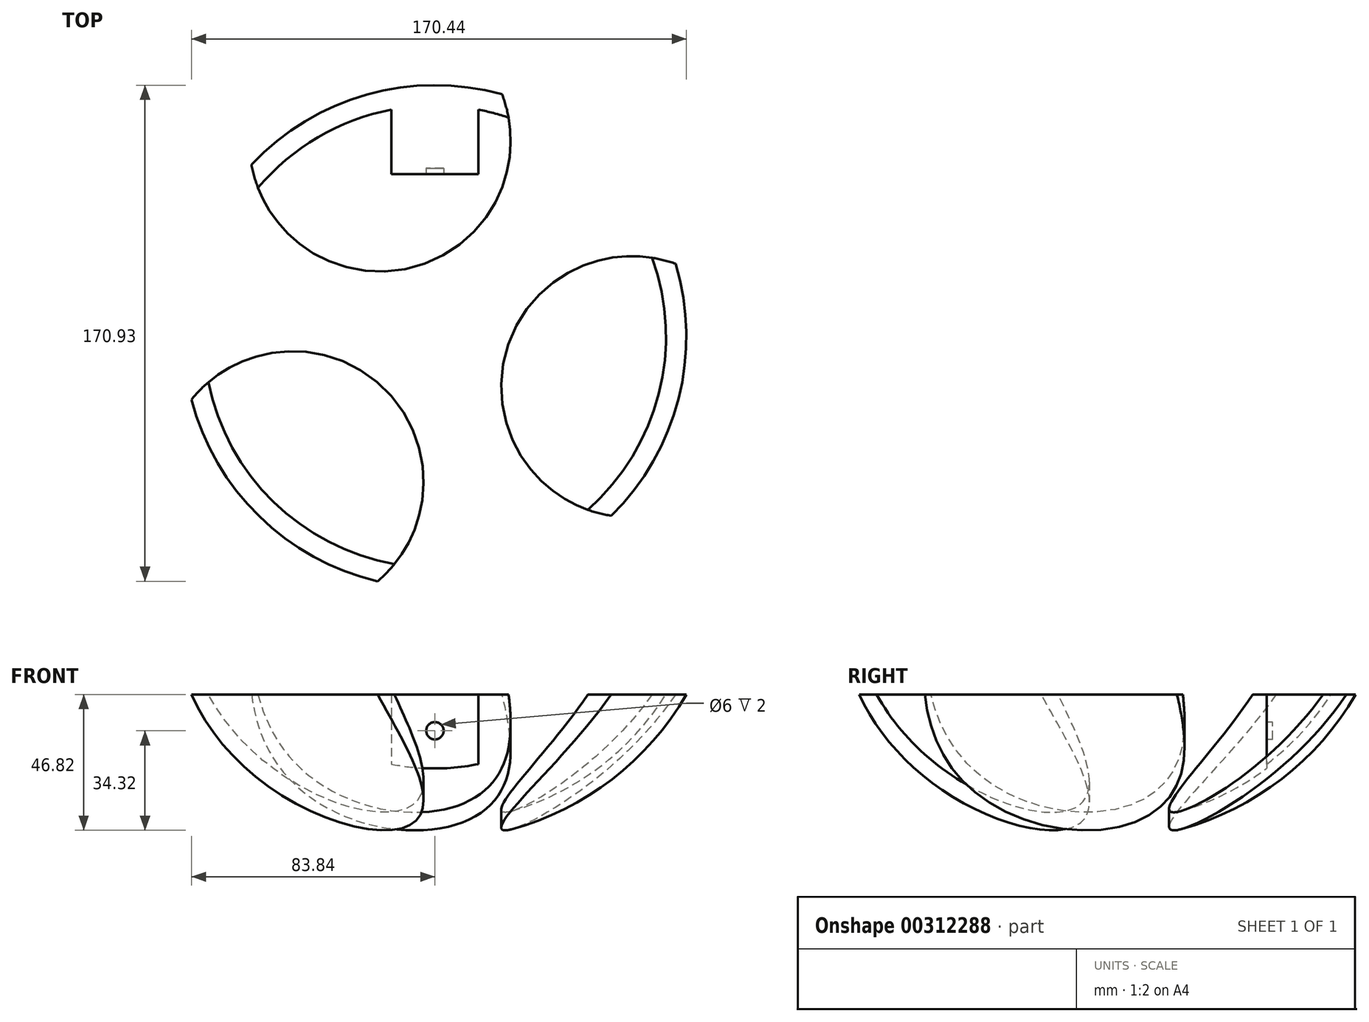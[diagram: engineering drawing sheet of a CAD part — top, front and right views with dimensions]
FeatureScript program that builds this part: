
annotation { "Feature Type Name" : "Feature", "Feature Type Description" : "" }
export const myFeature = defineFeature(function(context is Context, id is Id, definition is map)
    precondition{}
    {
        {
            var Q0;
            Q0=qCreatedBy(makeId("Front.planeOp"),FACE);
            var sketch = newSketch(context, id + "F0", { "sketchPlane" : qUnion([Q0])});
            skArc(sketch, "E0", {"start": v(-86.6, -50) * mm, "mid": v(-50, -86.6) * mm, "end": v(0, -100) * mm});
            skLineSegment(sketch, "E1", {"start": v(0, -50) * mm, "end": v(0, -100) * mm});
            skLineSegment(sketch, "E2", {"start": v(0, -50) * mm, "end": v(-86.6, -50) * mm});
            skPoint(sketch, "E3.orphan", {"position": v(0, 100) * mm});
            skSolve(sketch);
        }
        {
            var Q0;
            Q0=makeQuery(id+"F0.imprint","IMPRINT",FACE,{"disambiguationData":[TD([[makeQuery(id+"F0.imprint","IMPRINT",EDGE,{"derivedFrom":sQuery(id+"F0.wireOp",EDGE,"E0")}),1.0]])]});
            var Q1;
            Q1=sQuery(id+"F0.wireOp",EDGE,"E1");
            revolve(context, id + "F1", {"entities" : qUnion([Q0]), "axis" : qUnion([Q1]), "revolveType" : RevolveType.FULL});
        }
        {
            var Q0;
            Q0=makeQuery(id+"F1.opRevolve","SWEPT_FACE",FACE,{"disambiguationData":[OSD([sQuery(id+"F0.wireOp",EDGE,"E2")])]});
            shell(context, id + "F2", {"entities" : qUnion([Q0]), "thickness" : 6 * mm});
        }
        {
            var Q0;
            Q0=qCreatedBy(makeId("Front.planeOp"),FACE);
            cPlane(context, id + "F3", {"entities" : qUnion([Q0]), "cplaneType" : CPlaneType.OFFSET, "offset" : 56 * mm, "oppositeDirection" : true, "width" : 150 * mm, "height" : 150 * mm});
        }
        {
            var Q0;
            Q0=qCreatedBy(id+"F3.planeOp",FACE);
            var sketch = newSketch(context, id + "F4", { "sketchPlane" : qUnion([Q0])});
            skLineSegment(sketch, "E4.0", {"start": v(-15, -50) * mm, "end": v(15, -50) * mm});
            skLineSegment(sketch, "E5", {"start": v(-15, -50) * mm, "end": v(-15, -90) * mm});
            skLineSegment(sketch, "E6", {"start": v(-15, -90) * mm, "end": v(15, -90) * mm});
            skLineSegment(sketch, "E7", {"start": v(15, -90) * mm, "end": v(15, -50) * mm});
            skPoint(sketch, "E8.orphan", {"position": v(86.6, -50) * mm});
            skPoint(sketch, "E9.orphan", {"position": v(-86.6, -50) * mm});
            skSolve(sketch);
        }
        {
            var Q0;
            Q0=qSketchRegion(id+"F4",true);
            var Q1;
            Q1=makeQuery(id+"F2.opShell","OFFSET_FACE",FACE,{"disambiguationData":[OSD([sQuery(id+"F0.wireOp",EDGE,"E0")])]});
            extrude(context, id + "F5", {"entities" : qUnion([Q0]), "operationType" : NewBodyOperationType.ADD, "endBound" : BoundingType.UP_TO_SURFACE, "oppositeDirection" : true, "endBoundEntityFace" : qUnion([Q1]), "depth" : 25 * mm});
        }
        {
            var Q0;
            Q0=makeQuery(id+"F5.opExtrude","CAP_FACE",FACE,{"disambiguationData":[OSD([sQuery(id+"F4.wireOp",EDGE,"E4.0"),sQuery(id+"F4.wireOp",EDGE,"E5"),sQuery(id+"F4.wireOp",EDGE,"E6"),sQuery(id+"F4.wireOp",EDGE,"E7")])],"isStart":true});
            var sketch = newSketch(context, id + "F6", { "sketchPlane" : qUnion([Q0])});
            skCircle(sketch, "E10", {"center": v(0, -62.5) * mm, "radius": 3 * mm});
            skSolve(sketch);
        }
        {
            var Q0;
            Q0=qSketchRegion(id+"F6",true);
            extrude(context, id + "F7", {"entities" : qUnion([Q0]), "operationType" : NewBodyOperationType.REMOVE, "oppositeDirection" : true, "depth" : 2 * mm});
        }
        {
            var Q0;
            Q0=qCreatedBy(makeId("Top.planeOp"),FACE);
            cPlane(context, id + "F8", {"entities" : qUnion([Q0]), "cplaneType" : CPlaneType.OFFSET, "offset" : 100 * mm, "oppositeDirection" : true, "width" : 150 * mm, "height" : 150 * mm});
        }
        {
            var Q0;
            Q0=qCreatedBy(id+"F8.planeOp",FACE);
            var sketch = newSketch(context, id + "F9", { "sketchPlane" : qUnion([Q0])});
            skArc(sketch, "E11.0", {"start": v(82.9, 25.08) * mm, "mid": v(60.51, 61.95) * mm, "end": v(23.12, 83.46) * mm});
            skArc(sketch, "E12", {"start": v(-19.72, -84.33) * mm, "mid": v(-17.47, -17.88) * mm, "end": v(-83.84, -21.7) * mm});
            skArc(sketch, "E13", {"start": v(82.9, 25.08) * mm, "mid": v(24.22, -6.19) * mm, "end": v(60.72, -61.75) * mm});
            skArc(sketch, "E14", {"start": v(-63.17, 59.24) * mm, "mid": v(-6.75, 24.07) * mm, "end": v(23.12, 83.46) * mm});
            skPoint(sketch, "E15.orphan", {"position": v(-97.82, -100.15) * mm});
            skPoint(sketch, "E16.trimOffspring.end.orphan", {"position": v(135.65, -34.64) * mm});
            skPoint(sketch, "E17.trimOffspring.end.orphan", {"position": v(-37.83, 134.8) * mm});
            skArc(sketch, "E18.trimOffspring", {"start": v(-63.17, 59.24) * mm, "mid": v(-83.9, 21.43) * mm, "end": v(-83.84, -21.7) * mm});
            skArc(sketch, "E19.trimOffspring", {"start": v(-19.72, -84.33) * mm, "mid": v(23.4, -83.38) * mm, "end": v(60.72, -61.75) * mm});
            skSolve(sketch);
        }
        {
            var Q0;
            Q0=qSketchRegion(id+"F9",true);
            extrude(context, id + "F10", {"entities" : qUnion([Q0]), "operationType" : NewBodyOperationType.REMOVE, "endBound" : BoundingType.THROUGH_ALL, "depth" : 25 * mm});
        }
    });
